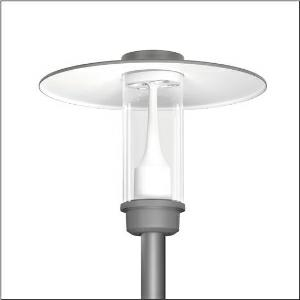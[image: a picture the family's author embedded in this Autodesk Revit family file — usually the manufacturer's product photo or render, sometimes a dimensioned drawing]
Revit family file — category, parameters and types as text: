
# Revit family: litepole_2_iq___p1_0a_5xa5425lf14h_94a7
name_source: partatom
category: Lighting Fixtures
units: mm (PartAtom-declared; Revit-internal decimal feet)

## family parameters
Cut with Voids When Loaded = No
Host = Face
Light Source = No
Part Type = Normal
Room Calculation Point = No
Round Connector Dimension = Use Diameter
Shared = No

## types (1)
- --- (1 x LED, 1520 lm, 10 W, 4000K)
    Apparent Load = 10 VA
    CIE Flux Codes = 33 62 89 96 100
    Color Rendering = 70
    Color Temperature = 4000K
    Default Elevation = 1800 mm
    Description = Litepole 2 iQ, mast luminaire, Module 540 iQ-SR, primary light control with 3 zone facetted reflector, of plastic, silver coated, highly specular, structured, primary optical cover: cover, of PMMA, transparent, light distribution: P1.0a, light emission: direct distribution, primary light characteristic: strongly asymmetric, installation type: post-top, LED, High Power LED, rated luminous flux: 1.520lm, luminous efficacy: 152lm/W, light colour: 740, colour temperature: 4000K, control gear: iQ Street-Remote, control: pre-setting: logarithmic dimming characteristic, Street-Remote, Auto-Match, Temp-Guard, Lumen-Switch, Night-Set, Smart-Wire, Light-Fading, Desk-Remote (wireless, voltage-free reading and setting of iQ features in the workshop via application-optimized NFC function/RFID function), optimised constant luminous flux control (CLO 2.0), with terminal, 6-pole, max. 2.5mm², mains connection: 230..240V, AC, 50/60Hz, start of lifetime: 10W, end of service life: 10W, reduction: 5W, luminaire housing, upper part, of aluminium, coated, Siteco® metallic grey (DB 702S), diameter: 750mm, height: 590mm, spigot size: d x l = 76 x 70mm (post-top) | with reducer (optional accessory) 60 x 70mm, mounting height: 3..5m, post-top mast mounting element, of diecast aluminium, coated, Siteco® metallic grey (DB 702S), Module 540 iQ-SR, traffic white (RAL 9016), equipment: standard, protection rating (complete): IP65, insulation class (complete): insulation class II (safety insulation), certification: CE, ENEC, VDE, packaging unit: 1 piece

Light Distribution: P1.0a
    Height = 590 mm
    Lamp = 1 x LED
    Lamp Light Flux = 1520 lm
    Lamp Power = 10 W
    Lamp count = 1
    Length = 750 mm
    Luminous efficacy = 152 lm/W
    Manufacturer = Siteco
    ModVariant = No
    Model = 5XA5425LF14H
    Number of Poles = 1
    OnlyDefault = Yes
    Power Factor = 1
    Product Name = Litepole 2 iQ | P1.0a
    Product group = mast luminaire | pylon top
    ProductGroupID = 6100
    Protection Class = Protection class II
    Protection Degree = IP 65
    RLX_Detail_Level = 1
    RLX_Emergency_Light_Flux = 0 lm
    RLX_Emergency_Type = 0
    RLX_Emergency_Type_DB = No
    RlxData = <blob elided: 59677 chars, md5=41519145>
    Socket = socket
    Standby Power = 0 W
    System Light Flux = 1520 lm
    System Power = 10 W
    Type Comments = factory setting: luminous flux: 100 % | dim-lin: 254 | 401 mA
    Type Image = l_1006518.jpg
    URL = http://relux.com
    VarID = @adj_192480
    Voltage = 0 V
    Weight = 0.00 kg
    Width = 0 mm  [stored 0 ft]

note: [stored X ft] marks values corroborated as IEEE doubles in the binary element streams (Revit-internal decimal feet)

## geometry (parser evidence)
native form markers: Blend x4, Sweep x9
no freeform markers — native parametric forms only
